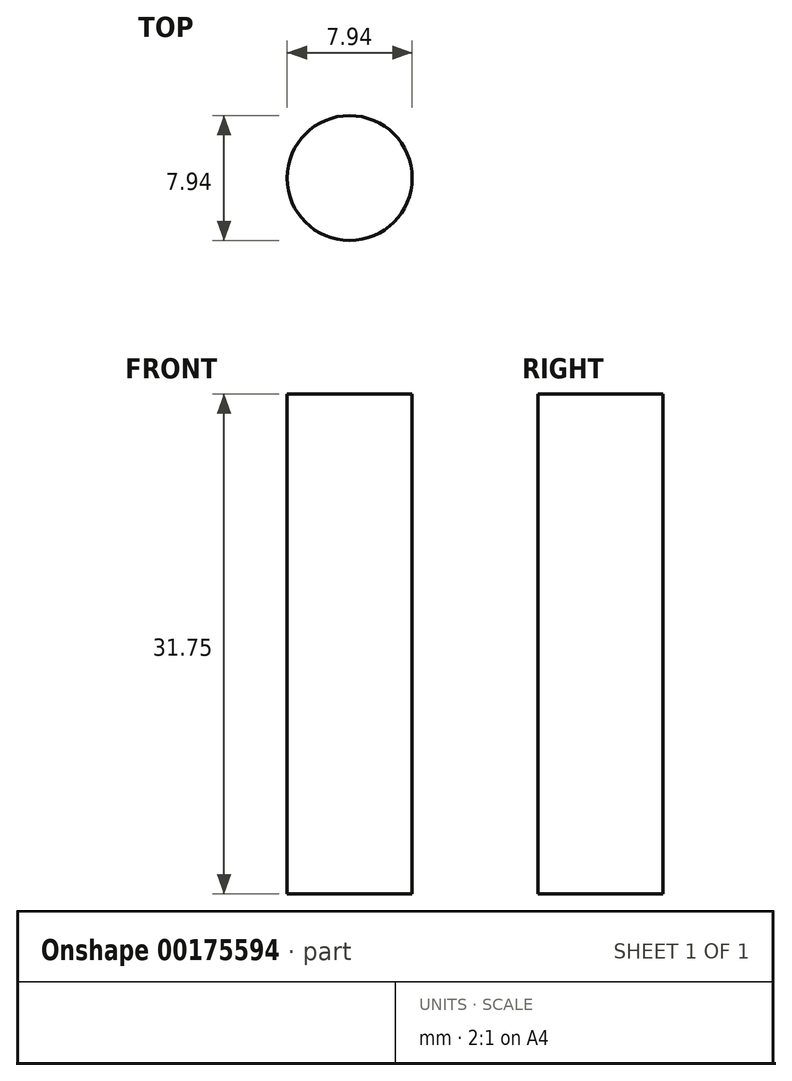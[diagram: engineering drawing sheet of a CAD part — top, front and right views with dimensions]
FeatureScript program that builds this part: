
annotation { "Feature Type Name" : "Feature", "Feature Type Description" : "" }
export const myFeature = defineFeature(function(context is Context, id is Id, definition is map)
    precondition{}
    {
        {
            var Q0;
            Q0=qCreatedBy(makeId("Top.planeOp"),FACE);
            var sketch = newSketch(context, id + "F0", { "sketchPlane" : qUnion([Q0])});
            skCircle(sketch, "E0", {"center": v(0, 0) * mm, "radius": 3.97 * mm});
            skSolve(sketch);
        }
        {
            var Q0;
            Q0=makeQuery(id+"F0.imprint","IMPRINT",FACE,{"disambiguationData":[TD([[makeQuery(id+"F0.imprint","IMPRINT",EDGE,{"derivedFrom":sQuery(id+"F0.wireOp",EDGE,"E0")}),1.0]])]});
            extrude(context, id + "F1", {"entities" : qUnion([Q0]), "depth" : 31.75 * mm});
        }
    });
